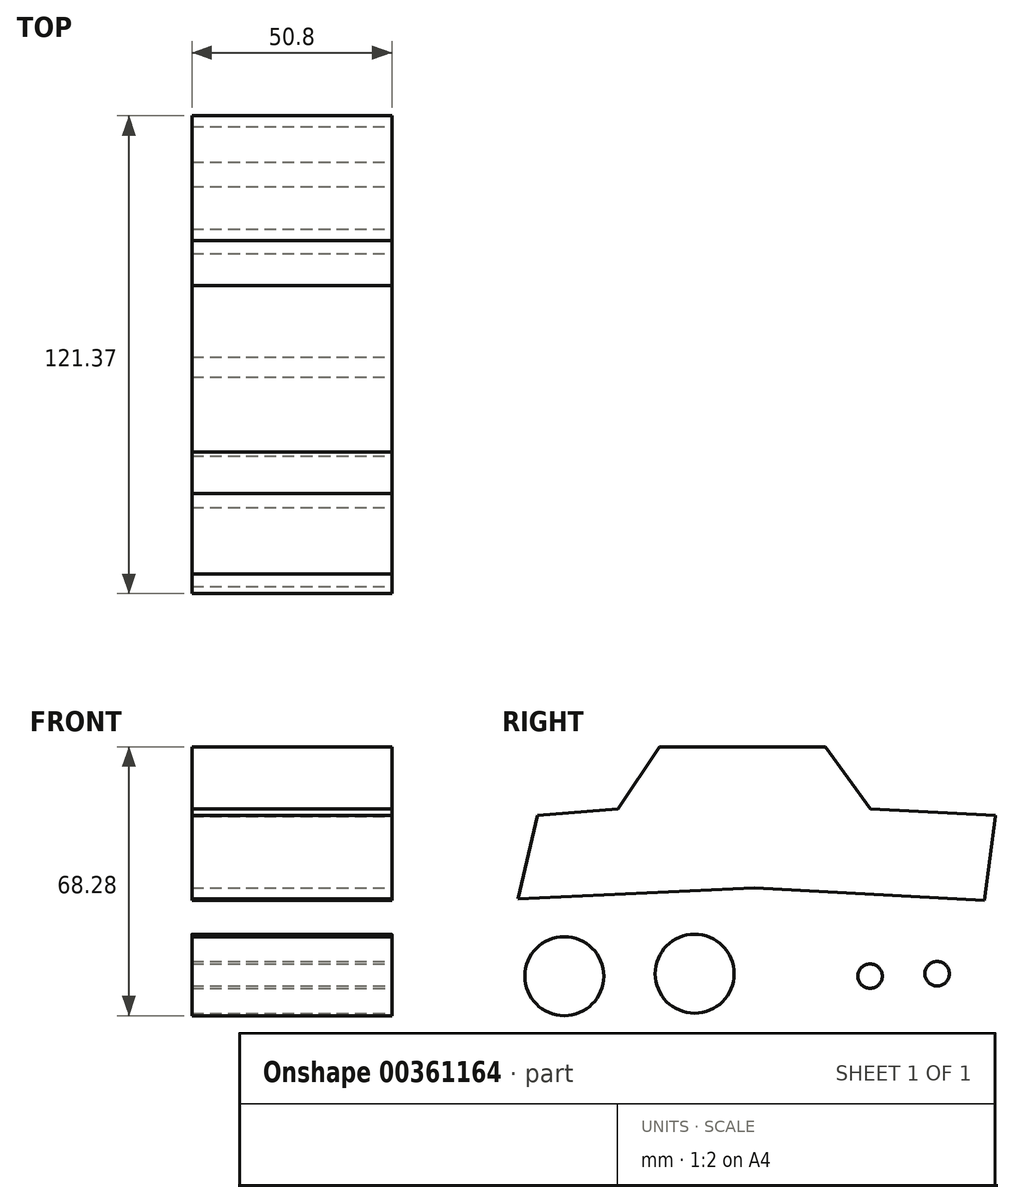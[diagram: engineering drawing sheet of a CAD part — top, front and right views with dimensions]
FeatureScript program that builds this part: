
annotation { "Feature Type Name" : "Feature", "Feature Type Description" : "" }
export const myFeature = defineFeature(function(context is Context, id is Id, definition is map)
    precondition{}
    {
        {
            var Q0;
            Q0=qCreatedBy(makeId("Right.planeOp"),FACE);
            var sketch = newSketch(context, id + "F0", { "sketchPlane" : qUnion([Q0])});
            skLineSegment(sketch, "E0", {"start": v(-60.1, 7.06) * mm, "end": v(0, 9.85) * mm});
            skLineSegment(sketch, "E1", {"start": v(0, 9.85) * mm, "end": v(58.5, 6.67) * mm});
            skLineSegment(sketch, "E2", {"start": v(-60.1, 7.06) * mm, "end": v(-55.1, 28.35) * mm});
            skLineSegment(sketch, "E3", {"start": v(-55.1, 28.35) * mm, "end": v(-34.67, 29.9) * mm});
            skLineSegment(sketch, "E4", {"start": v(-34.67, 29.9) * mm, "end": v(-24.15, 45.71) * mm});
            skLineSegment(sketch, "E5", {"start": v(-24.15, 45.71) * mm, "end": v(18.12, 45.71) * mm});
            skLineSegment(sketch, "E6", {"start": v(18.12, 45.71) * mm, "end": v(29.5, 29.9) * mm});
            skLineSegment(sketch, "E7", {"start": v(29.5, 29.9) * mm, "end": v(61.28, 28.35) * mm});
            skLineSegment(sketch, "E8", {"start": v(61.28, 28.35) * mm, "end": v(61.28, 28.06) * mm});
            skLineSegment(sketch, "E9", {"start": v(58.5, 6.67) * mm, "end": v(61.28, 28.06) * mm});
            skCircle(sketch, "E10", {"center": v(-48.28, -12.54) * mm, "radius": 10.03 * mm});
            skCircle(sketch, "E11", {"center": v(-15.17, -11.92) * mm, "radius": 10.03 * mm});
            skCircle(sketch, "E12", {"center": v(46.43, -11.92) * mm, "radius": 3.1 * mm});
            skCircle(sketch, "E13", {"center": v(29.4, -12.54) * mm, "radius": 3.1 * mm});
            skSolve(sketch);
        }
        {
            var Q0;
            Q0 = qSketchRegion(id + "F0", true);
            extrude(context, id + "F1", {"entities" : qUnion([Q0]), "oppositeDirection" : true, "depth" : 25.4 * mm});
        }
        {
            var Q0;
            Q0=qCreatedBy(makeId("Right.planeOp"),FACE);
            var sketch = newSketch(context, id + "F2", { "sketchPlane" : qUnion([Q0])});
            skLineSegment(sketch, "E14.0.0", {"start": v(0, 9.85) * mm, "end": v(58.5, 6.67) * mm});
            skLineSegment(sketch, "E14.0.1", {"start": v(58.5, 6.67) * mm, "end": v(61.28, 28.06) * mm});
            skLineSegment(sketch, "E14.0.2", {"start": v(61.28, 28.06) * mm, "end": v(61.28, 28.35) * mm});
            skLineSegment(sketch, "E14.0.3", {"start": v(61.28, 28.35) * mm, "end": v(29.5, 29.9) * mm});
            skLineSegment(sketch, "E14.0.4", {"start": v(29.5, 29.9) * mm, "end": v(18.12, 45.71) * mm});
            skLineSegment(sketch, "E14.0.5", {"start": v(18.12, 45.71) * mm, "end": v(-24.15, 45.71) * mm});
            skLineSegment(sketch, "E14.0.6", {"start": v(-24.15, 45.71) * mm, "end": v(-34.67, 29.9) * mm});
            skLineSegment(sketch, "E14.0.7", {"start": v(-34.67, 29.9) * mm, "end": v(-55.1, 28.35) * mm});
            skLineSegment(sketch, "E14.0.8", {"start": v(-55.1, 28.35) * mm, "end": v(-60.1, 7.06) * mm});
            skLineSegment(sketch, "E14.0.9", {"start": v(-60.1, 7.06) * mm, "end": v(0, 9.85) * mm});
            skCircle(sketch, "E15.0.0", {"center": v(-48.28, -12.54) * mm, "radius": 10.03 * mm});
            skCircle(sketch, "E16.0.0", {"center": v(-15.17, -11.92) * mm, "radius": 10.03 * mm});
            skCircle(sketch, "E17.0", {"center": v(46.43, -11.92) * mm, "radius": 3.1 * mm});
            skCircle(sketch, "E18.0", {"center": v(29.4, -12.54) * mm, "radius": 3.1 * mm});
            skSolve(sketch);
        }
        {
            var Q0;
            Q0 = qSketchRegion(id + "F2", true);
            extrude(context, id + "F3", {"entities" : qUnion([Q0]), "operationType" : NewBodyOperationType.ADD, "depth" : 25.4 * mm});
        }
    });
